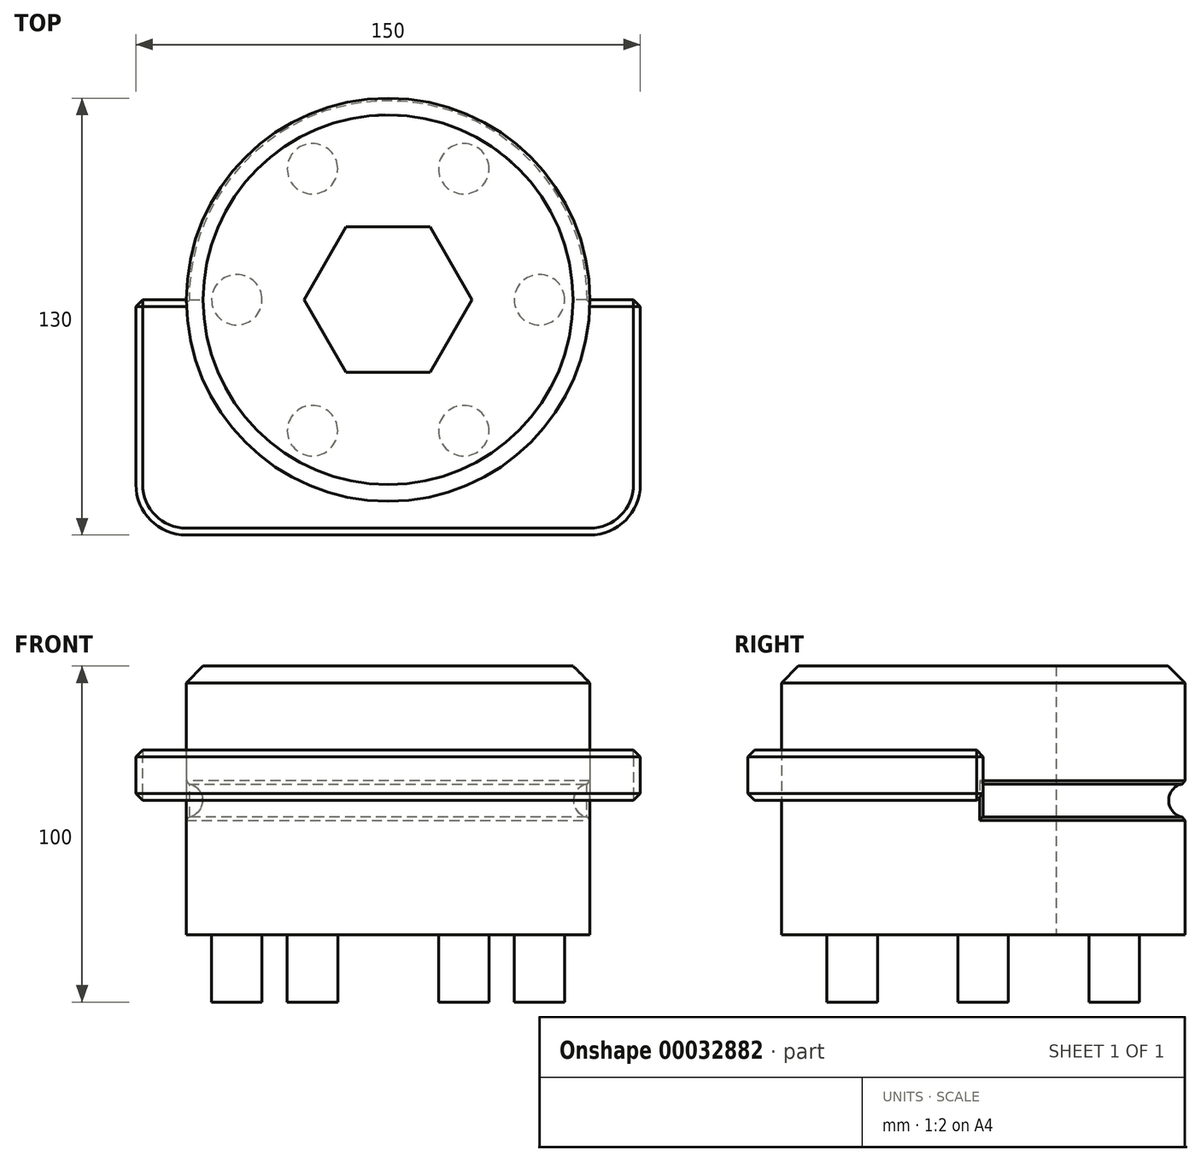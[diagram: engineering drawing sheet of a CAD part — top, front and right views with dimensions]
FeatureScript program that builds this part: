
annotation { "Feature Type Name" : "Feature", "Feature Type Description" : "" }
export const myFeature = defineFeature(function(context is Context, id is Id, definition is map)
    precondition{}
    {
        {
            var Q0;
            Q0=qCreatedBy(makeId("Top.planeOp"),FACE);
            var sketch = newSketch(context, id + "F0", { "sketchPlane" : qUnion([Q0])});
            skCircle(sketch, "E0", {"center": v(0, 0) * mm, "radius": 60 * mm});
            skLineSegment(sketch, "E1", {"start": v(-87.69, 0) * mm, "end": v(81.32, 0) * mm, "construction": true});
            skCircle(sketch, "E2", {"center": v(0, 0) * mm, "radius": 45 * mm, "construction": true});
            skSolve(sketch);
        }
        {
            var Q0;
            Q0=makeQuery(id+"F0.imprint","IMPRINT",FACE,{"disambiguationData":[TD([[makeQuery(id+"F0.imprint","IMPRINT",EDGE,{"derivedFrom":sQuery(id+"F0.wireOp",EDGE,"E0")}),1.0]])]});
            extrude(context, id + "F1", {"entities" : qUnion([Q0]), "depth" : 80 * mm});
        }
        {
            var Q0;
            Q0=makeQuery(id+"F0.imprint","IMPRINT",FACE,{"disambiguationData":[TD([[makeQuery(id+"F0.imprint","IMPRINT",EDGE,{"derivedFrom":sQuery(id+"F0.wireOp",EDGE,"E0")}),1.0]])]});
            var sketch = newSketch(context, id + "F2", { "sketchPlane" : qUnion([Q0])});
            skCircle(sketch, "E3", {"center": v(-45, 0) * mm, "radius": 7.5 * mm});
            skSolve(sketch);
        }
        {
            var Q0;
            Q0=makeQuery(id+"F2.imprint","IMPRINT",FACE,{"disambiguationData":[TD([[makeQuery(id+"F2.imprint","IMPRINT",EDGE,{"derivedFrom":sQuery(id+"F2.wireOp",EDGE,"E3")}),1.0]])]});
            extrude(context, id + "F3", {"entities" : qUnion([Q0]), "oppositeDirection" : true, "depth" : 20 * mm});
        }
        {
            var Q0;
            Q0=qCreatedBy(makeId("Right.planeOp"),FACE);
            var sketch = newSketch(context, id + "F4", { "sketchPlane" : qUnion([Q0])});
            skLineSegment(sketch, "E4", {"start": v(0, -67.97) * mm, "end": v(0, 92.5) * mm, "construction": true});
            skSolve(sketch);
        }
        {
            var Q0;
            Q0=makeQuery(id+"F3.opExtrude","SWEPT_BODY",BODY,{"disambiguationData":[OSD([sQuery(id+"F2.wireOp",EDGE,"E3")])]});
            var Q1;
            Q1=sQuery(id+"F4.wireOp",EDGE,"E4");
            circularPattern(context, id + "F5", {"entities" : qUnion([Q0]), "axis" : qUnion([Q1]), "angle" : 60 * degree, "instanceCount" : 6});
        }
        {
            var Q0;
            Q0=makeQuery(id+"F0.imprint","IMPRINT",FACE,{"disambiguationData":[TD([[makeQuery(id+"F0.imprint","IMPRINT",EDGE,{"derivedFrom":sQuery(id+"F0.wireOp",EDGE,"E0")}),1.0]])]});
            var sketch = newSketch(context, id + "F6", { "sketchPlane" : qUnion([Q0])});
            skCircle(sketch, "E5.cCircle", {"center": v(0, 0) * mm, "radius": 25 * mm, "construction": true});
            skLineSegment(sketch, "E5.0", {"start": v(25, 0) * mm, "end": v(12.5, -21.65) * mm});
            skLineSegment(sketch, "E5.1", {"start": v(12.5, -21.65) * mm, "end": v(-12.5, -21.65) * mm});
            skLineSegment(sketch, "E5.2", {"start": v(-12.5, -21.65) * mm, "end": v(-25, 0) * mm});
            skLineSegment(sketch, "E5.3", {"start": v(-25, 0) * mm, "end": v(-12.5, 21.65) * mm});
            skLineSegment(sketch, "E5.4", {"start": v(-12.5, 21.65) * mm, "end": v(12.5, 21.65) * mm});
            skLineSegment(sketch, "E5.5", {"start": v(12.5, 21.65) * mm, "end": v(25, 0) * mm});
            skSolve(sketch);
        }
        {
            var Q0;
            Q0=makeQuery(id+"F6.imprint","IMPRINT",FACE,{"disambiguationData":[TD([[makeQuery(id+"F6.imprint","IMPRINT",EDGE,{"derivedFrom":sQuery(id+"F6.wireOp",EDGE,"E5.0")}),-1.0]])]});
            extrude(context, id + "F7", {"entities" : qUnion([Q0]), "operationType" : NewBodyOperationType.REMOVE, "endBound" : BoundingType.UP_TO_NEXT, "depth" : 25 * mm});
        }
        {
            var Q0;
            Q0=qCreatedBy(makeId("Top.planeOp"),FACE);
            cPlane(context, id + "F8", {"entities" : qUnion([Q0]), "cplaneType" : CPlaneType.OFFSET, "offset" : 40 * mm, "width" : 150 * mm, "height" : 150 * mm});
        }
        {
            var Q0;
            Q0=qCreatedBy(makeId("Front.planeOp"),FACE);
            var sketch = newSketch(context, id + "F9", { "sketchPlane" : qUnion([Q0])});
            skLineSegment(sketch, "E6", {"start": v(-69.58, 40) * mm, "end": v(-44.07, 40) * mm, "construction": true});
            skCircle(sketch, "E7", {"center": v(-60.16, 40) * mm, "radius": 5 * mm});
            skSolve(sketch);
        }
        {
            var Q0;
            Q0=makeQuery(id+"F9.imprint","IMPRINT",FACE,{"disambiguationData":[TD([[makeQuery(id+"F9.imprint","IMPRINT",EDGE,{"derivedFrom":sQuery(id+"F9.wireOp",EDGE,"E7")}),1.0]])]});
            var Q1;
            Q1=sQuery(id+"F4.wireOp",EDGE,"E4");
            revolve(context, id + "F10", {"operationType" : NewBodyOperationType.REMOVE, "entities" : qUnion([Q0]), "axis" : qUnion([Q1]), "revolveType" : RevolveType.ONE_DIRECTION, "oppositeDirection" : true, "angle" : 180 * degree});
        }
        {
            var Q0;
            Q0=makeQuery(id+"F1.opExtrude","CAP_EDGE",EDGE,{"disambiguationData":[OSD([sQuery(id+"F0.wireOp",EDGE,"E0")])],"isStart":false});
            chamfer(context, id + "F11", {"entities" : qUnion([Q0]), "width" : 5 * mm});
        }
        {
            var Q0;
            Q0=makeQuery(id+"F10.boolean.opBoolean","INTERSECT",EDGE,{"disambiguationData":[OD(0.0)],"derivedFrom":[makeQuery(id+"F1.opExtrude","SWEPT_FACE",FACE,{"disambiguationData":[OSD([sQuery(id+"F0.wireOp",EDGE,"E0")])]}),makeQuery(id+"F10.opRevolve","SWEPT_FACE",FACE,{"disambiguationData":[OSD([sQuery(id+"F9.wireOp",EDGE,"E7")])]})]});
            var Q1;
            Q1=makeQuery(id+"F10.boolean.opBoolean","INTERSECT",EDGE,{"disambiguationData":[OD(1.0)],"derivedFrom":[makeQuery(id+"F1.opExtrude","SWEPT_FACE",FACE,{"disambiguationData":[OSD([sQuery(id+"F0.wireOp",EDGE,"E0")])]}),makeQuery(id+"F10.opRevolve","SWEPT_FACE",FACE,{"disambiguationData":[OSD([sQuery(id+"F9.wireOp",EDGE,"E7")])]})]});
            chamfer(context, id + "F12", {"entities" : qUnion([Q0, Q1]), "width" : 1 * mm, "tangentPropagation" : true});
        }
        {
            var Q0;
            Q0=makeQuery(id+"F10.boolean.opBoolean","INTERSECT",EDGE,{"derivedFrom":[makeQuery(id+"F1.opExtrude","SWEPT_FACE",FACE,{"disambiguationData":[OSD([sQuery(id+"F0.wireOp",EDGE,"E0")])]}),makeQuery(id+"F10.opRevolve","CAP_FACE",FACE,{"disambiguationData":[OSD([sQuery(id+"F9.wireOp",EDGE,"E7")])],"isStart":true})]});
            var Q1;
            Q1=makeQuery(id+"F10.boolean.opBoolean","INTERSECT",EDGE,{"derivedFrom":[makeQuery(id+"F1.opExtrude","SWEPT_FACE",FACE,{"disambiguationData":[OSD([sQuery(id+"F0.wireOp",EDGE,"E0")])]}),makeQuery(id+"F10.opRevolve","CAP_FACE",FACE,{"disambiguationData":[OSD([sQuery(id+"F9.wireOp",EDGE,"E7")])],"isStart":false})]});
            chamfer(context, id + "F13", {"entities" : qUnion([Q0, Q1]), "width" : 1 * mm, "tangentPropagation" : true});
        }
        {
            var Q0;
            Q0=qCreatedBy(id+"F8.planeOp",FACE);
            var sketch = newSketch(context, id + "F14", { "sketchPlane" : qUnion([Q0])});
            skLineSegment(sketch, "E8", {"start": v(-60, 0) * mm, "end": v(-75, 0) * mm});
            skLineSegment(sketch, "E9", {"start": v(-75, 0) * mm, "end": v(-75, -55) * mm});
            skLineSegment(sketch, "E10", {"start": v(-60, -70) * mm, "end": v(60, -70) * mm});
            skLineSegment(sketch, "E11", {"start": v(75, -55) * mm, "end": v(75, 0) * mm});
            skLineSegment(sketch, "E12", {"start": v(75, 0) * mm, "end": v(60, 0) * mm});
            skArc(sketch, "E13", {"start": v(-60, 0) * mm, "mid": v(0, -60) * mm, "end": v(60, 0) * mm});
            skPoint(sketch, "E14.visualSharp", {"position": v(75, -70) * mm});
            skArc(sketch, "E14.filletArc", {"start": v(60, -70) * mm, "mid": v(70.6, -65.6) * mm, "end": v(75, -55) * mm});
            skPoint(sketch, "E15.visualSharp", {"position": v(-75, -70) * mm});
            skArc(sketch, "E15.filletArc", {"start": v(-75, -55) * mm, "mid": v(-70.6, -65.6) * mm, "end": v(-60, -70) * mm});
            skSolve(sketch);
        }
        {
            var Q0;
            Q0=makeQuery(id+"F14.imprint","IMPRINT",FACE,{"disambiguationData":[TD([[makeQuery(id+"F14.imprint","IMPRINT",EDGE,{"derivedFrom":sQuery(id+"F14.wireOp",EDGE,"E8")}),1.0]])]});
            extrude(context, id + "F15", {"entities" : qUnion([Q0]), "depth" : 15 * mm});
        }
        {
            var Q0;
            Q0=makeQuery(id+"F15.opExtrude","CAP_EDGE",EDGE,{"disambiguationData":[OSD([sQuery(id+"F14.wireOp",EDGE,"E11")])],"isStart":false});
            var Q1;
            Q1=makeQuery(id+"F15.opExtrude","CAP_EDGE",EDGE,{"disambiguationData":[OSD([sQuery(id+"F14.wireOp",EDGE,"E11")])],"isStart":true});
            var Q2;
            Q2=makeQuery(id+"F15.opExtrude","SWEPT_EDGE",EDGE,{"disambiguationData":[OSD([sQuery(id+"F14.wireOp",EDGE,"E11"),sQuery(id+"F14.wireOp",EDGE,"E12")])]});
            var Q3;
            Q3=makeQuery(id+"F15.opExtrude","SWEPT_EDGE",EDGE,{"disambiguationData":[OSD([sQuery(id+"F14.wireOp",EDGE,"E8"),sQuery(id+"F14.wireOp",EDGE,"E9")])]});
            var Q4;
            Q4=makeQuery(id+"F15.opExtrude","CAP_EDGE",EDGE,{"disambiguationData":[OSD([sQuery(id+"F14.wireOp",EDGE,"E8")])],"isStart":false});
            var Q5;
            Q5=makeQuery(id+"F15.opExtrude","CAP_EDGE",EDGE,{"disambiguationData":[OSD([sQuery(id+"F14.wireOp",EDGE,"E8")])],"isStart":true});
            var Q6;
            Q6=makeQuery(id+"F15.opExtrude","CAP_EDGE",EDGE,{"disambiguationData":[OSD([sQuery(id+"F14.wireOp",EDGE,"E12")])],"isStart":false});
            var Q7;
            Q7=makeQuery(id+"F15.opExtrude","CAP_EDGE",EDGE,{"disambiguationData":[OSD([sQuery(id+"F14.wireOp",EDGE,"E12")])],"isStart":true});
            chamfer(context, id + "F16", {"entities" : qUnion([Q0, Q1, Q2, Q3, Q4, Q5, Q6, Q7]), "width" : 2 * mm, "tangentPropagation" : true});
        }
    });
